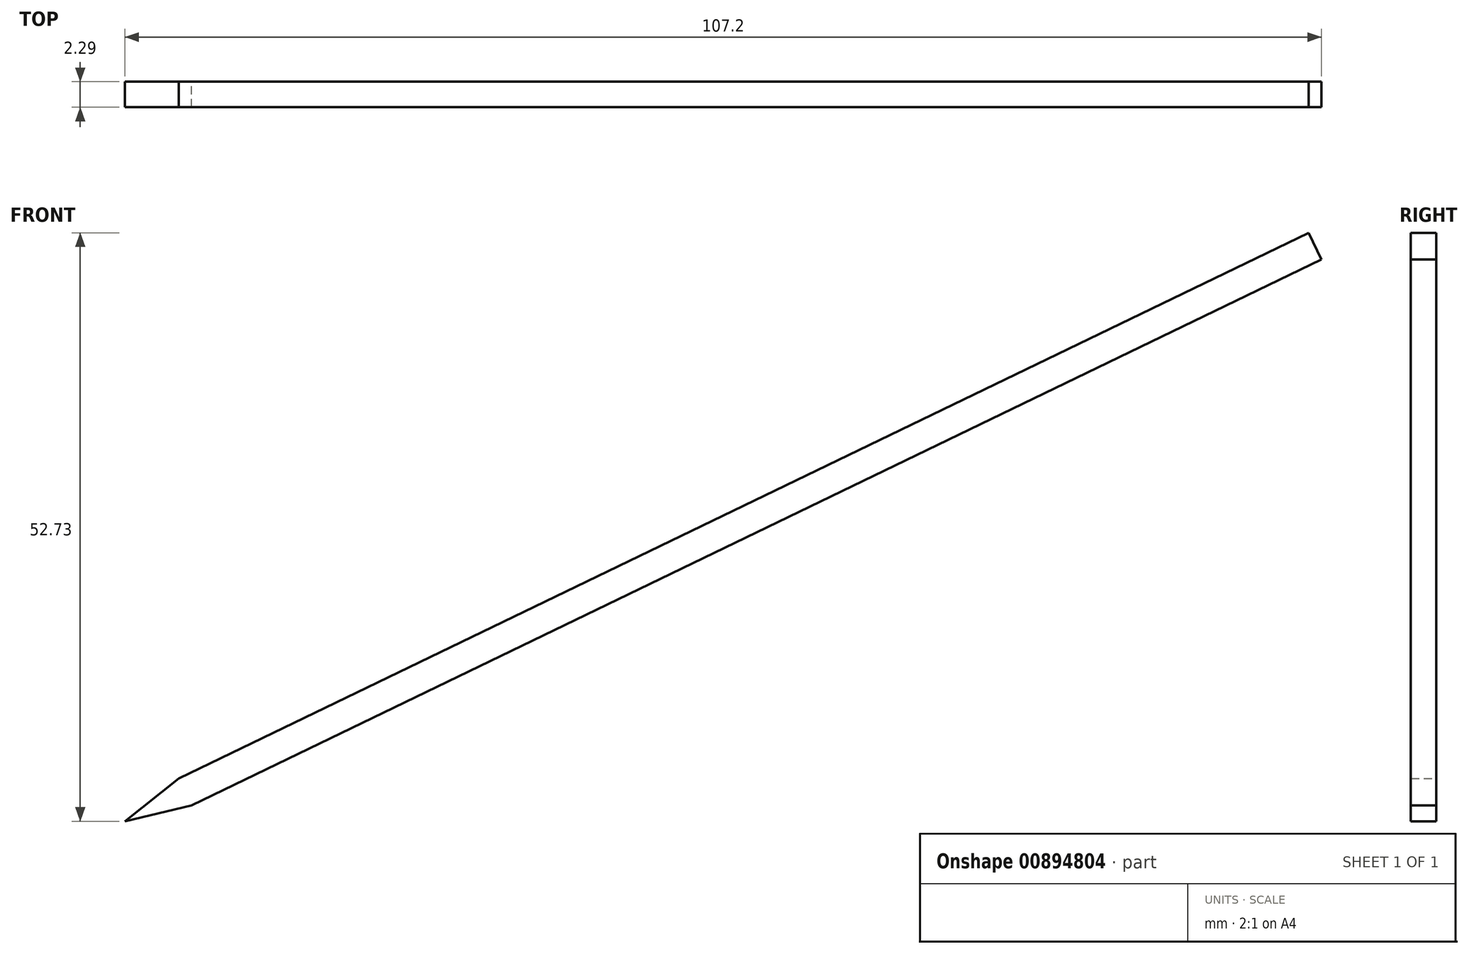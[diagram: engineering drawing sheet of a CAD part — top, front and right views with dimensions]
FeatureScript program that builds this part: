
annotation { "Feature Type Name" : "Feature", "Feature Type Description" : "" }
export const myFeature = defineFeature(function(context is Context, id is Id, definition is map)
    precondition{}
    {
        {
            var Q0;
            Q0=qCreatedBy(makeId("Front.planeOp"),FACE);
            var sketch = newSketch(context, id + "F0", { "sketchPlane" : qUnion([Q0])});
            skLineSegment(sketch, "E0", {"start": v(38.12, 17.7) * mm, "end": v(-63.1, -31.22) * mm});
            skLineSegment(sketch, "E1", {"start": v(-63.1, -31.22) * mm, "end": v(-67.92, -35.04) * mm});
            skLineSegment(sketch, "E2.MirrorCS", {"start": v(39.28, 15.29) * mm, "end": v(-61.94, -33.63) * mm});
            skLineSegment(sketch, "E3.MirrorCS", {"start": v(-61.94, -33.63) * mm, "end": v(-67.92, -35.04) * mm});
            skLineSegment(sketch, "E4", {"start": v(38.12, 17.7) * mm, "end": v(39.28, 15.29) * mm});
            skSolve(sketch);
        }
        {
            var Q0;
            Q0=makeQuery(id+"F0.imprint","IMPRINT",FACE,{"disambiguationData":[TD([[makeQuery(id+"F0.imprint","IMPRINT",EDGE,{"derivedFrom":sQuery(id+"F0.wireOp",EDGE,"E0")}),1.0]])]});
            extrude(context, id + "F1", {"entities" : qUnion([Q0]), "depth" : 2.3 * mm, "offsetDistance" : 25.4 * mm});
        }
        {
            var Q0;
            Q0=makeQuery(id+"F1.opExtrude","CAP_FACE",FACE,{"disambiguationData":[OSD([sQuery(id+"F0.wireOp",EDGE,"E0"),sQuery(id+"F0.wireOp",EDGE,"E1"),sQuery(id+"F0.wireOp",EDGE,"E2.MirrorCS"),sQuery(id+"F0.wireOp",EDGE,"E3.MirrorCS"),sQuery(id+"F0.wireOp",EDGE,"E4")])],"isStart":false});
            extrude(context, id + "F2", {"entities" : qUnion([Q0]), "operationType" : NewBodyOperationType.ADD, "oppositeDirection" : true, "depth" : 2.3 * mm, "offsetDistance" : 25.4 * mm});
        }
    });
